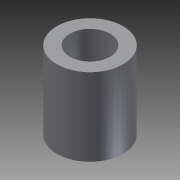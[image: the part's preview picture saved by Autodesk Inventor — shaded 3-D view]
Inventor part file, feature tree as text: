
AUTODESK INVENTOR PART (.ipt)
format: ipt  version: 2014 SP1 (Build 180222100, 222)  size: 97,280 bytes
history: native  units: in
note: dims shown in document units (in); Inventor stores cm internally (conversion verified against a paired STEP export)
features: extrude x2, sketch x2, other x1, imported_body x1
ambient origin geometry x8: Origin, YZ Plane, XZ Plane, XY Plane, X Axis, Y Axis, Z Axis, Center Point
bodies: Body1 (feature_tree)
feature tree (6):
  parser-record x1  (decoder bookkeeping rows leaked as tree rows — omitted from the tree; the rows remain in map.json)
  imported_body  "Base1"
  extrude  "Extrusion1"  Depth=1.0in TaperAngle=0.0deg
  extrude  "Extrusion2"  [1 undecoded]
  sketch  "Sketch1"  dims[d0=0.32in d1=1.0in d2=0.0in]
  sketch  "Sketch2"  dims[d3=0.125in d4=0.0in]
note: 1 required parameter value undecoded (feature->parameter linkage not recoverable at this tier; creation-order binding heuristic only, values carry confidence <= 0.55)
